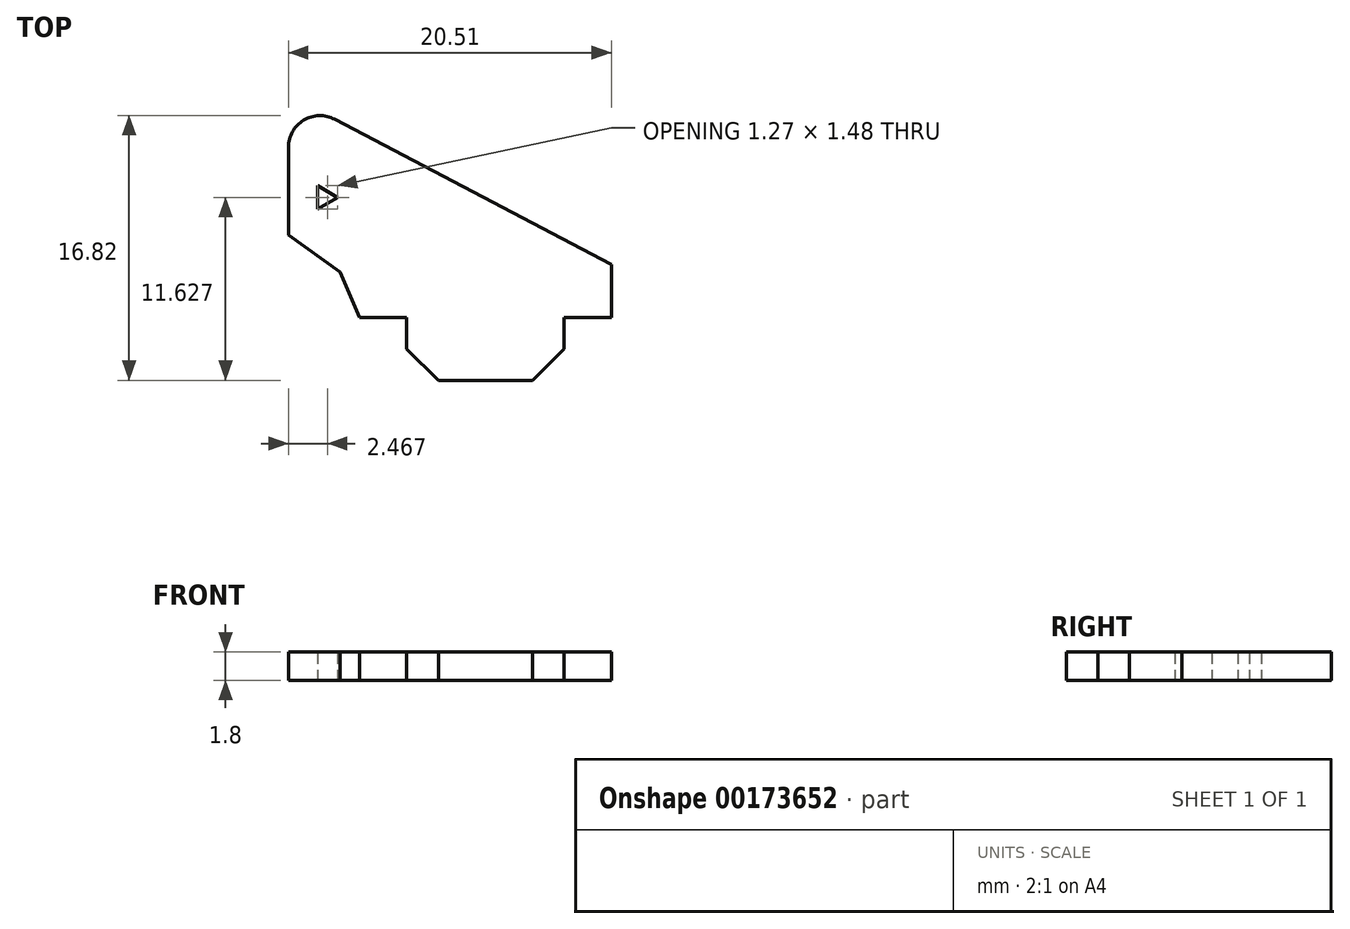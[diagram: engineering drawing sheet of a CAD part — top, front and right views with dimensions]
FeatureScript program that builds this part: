
annotation { "Feature Type Name" : "Feature", "Feature Type Description" : "" }
export const myFeature = defineFeature(function(context is Context, id is Id, definition is map)
    precondition{}
    {
        {
            var Q0;
            Q0=qCreatedBy(makeId("Top.planeOp"),FACE);
            var sketch = newSketch(context, id + "F0", { "sketchPlane" : qUnion([Q0])});
            skLineSegment(sketch, "E0", {"start": v(-14.2, 8.73) * mm, "end": v(-11.2, 8.73) * mm});
            skLineSegment(sketch, "E1", {"start": v(-11.2, 8.73) * mm, "end": v(-11.2, 6.73) * mm});
            skLineSegment(sketch, "E2", {"start": v(-11.2, 6.73) * mm, "end": v(-11.2, 4.73) * mm, "construction": true});
            skLineSegment(sketch, "E3", {"start": v(-11.2, 4.73) * mm, "end": v(-9.2, 4.73) * mm, "construction": true});
            skLineSegment(sketch, "E4", {"start": v(-11.2, 8.73) * mm, "end": v(-1.2, 8.73) * mm, "construction": true});
            skLineSegment(sketch, "E5", {"start": v(-1.2, 8.73) * mm, "end": v(1.8, 8.73) * mm});
            skLineSegment(sketch, "E6", {"start": v(-1.2, 8.73) * mm, "end": v(-1.2, 6.73) * mm});
            skLineSegment(sketch, "E7", {"start": v(-1.2, 6.73) * mm, "end": v(-1.2, 4.73) * mm, "construction": true});
            skLineSegment(sketch, "E8", {"start": v(-1.2, 4.73) * mm, "end": v(-3.2, 4.73) * mm, "construction": true});
            skLineSegment(sketch, "E9", {"start": v(-9.2, 4.73) * mm, "end": v(-3.2, 4.73) * mm});
            skLineSegment(sketch, "E10", {"start": v(-1.2, 6.73) * mm, "end": v(-3.2, 4.73) * mm});
            skLineSegment(sketch, "E11", {"start": v(1.8, 8.73) * mm, "end": v(1.8, 12.07) * mm});
            skCircle(sketch, "E12", {"center": v(-1.2, 8.73) * mm, "radius": 22.5 * mm, "construction": true});
            skCircle(sketch, "E13", {"center": v(-11.2, 8.73) * mm, "radius": 16 * mm, "construction": true});
            skLineSegment(sketch, "E14", {"start": v(1.8, 12.07) * mm, "end": v(-15.79, 21.32) * mm});
            skPoint(sketch, "E15.visualSharp", {"position": v(-18.72, 22.86) * mm});
            skArc(sketch, "E15.filletArc", {"start": v(-15.79, 21.32) * mm, "mid": v(-17.75, 21.26) * mm, "end": v(-18.72, 19.55) * mm});
            skCircle(sketch, "E16", {"center": v(-18.72, 12.86) * mm, "radius": 3.5 * mm, "construction": true});
            skLineSegment(sketch, "E17", {"start": v(-18.72, 16.36) * mm, "end": v(-16.47, 16.36) * mm, "construction": true});
            skCircle(sketch, "E18", {"center": v(-16.47, 16.36) * mm, "radius": 0.85 * mm, "construction": true});
            skLineSegment(sketch, "E19", {"start": v(-11.2, 6.73) * mm, "end": v(-9.2, 4.73) * mm});
            skLineSegment(sketch, "E20", {"start": v(-16.89, 17.1) * mm, "end": v(-16.89, 15.62) * mm});
            skLineSegment(sketch, "E21", {"start": v(-16.89, 15.62) * mm, "end": v(-15.62, 16.35) * mm});
            skLineSegment(sketch, "E22", {"start": v(-15.62, 16.35) * mm, "end": v(-16.89, 17.1) * mm});
            skLineSegment(sketch, "E23", {"start": v(-14.2, 8.73) * mm, "end": v(-15.44, 11.62) * mm});
            skLineSegment(sketch, "E24", {"start": v(-18.72, 19.55) * mm, "end": v(-18.72, 13.98) * mm});
            skLineSegment(sketch, "E25", {"start": v(-15.44, 11.62) * mm, "end": v(-18.72, 13.98) * mm});
            skSolve(sketch);
        }
        {
            var Q0;
            Q0=makeQuery(id+"F0.imprint","IMPRINT",FACE,{"disambiguationData":[TD([[makeQuery(id+"F0.imprint","IMPRINT",EDGE,{"derivedFrom":sQuery(id+"F0.wireOp",EDGE,"E0")}),1.0]])]});
            extrude(context, id + "F1", {"entities" : qUnion([Q0]), "depth" : 1.8 * mm});
        }
    });
